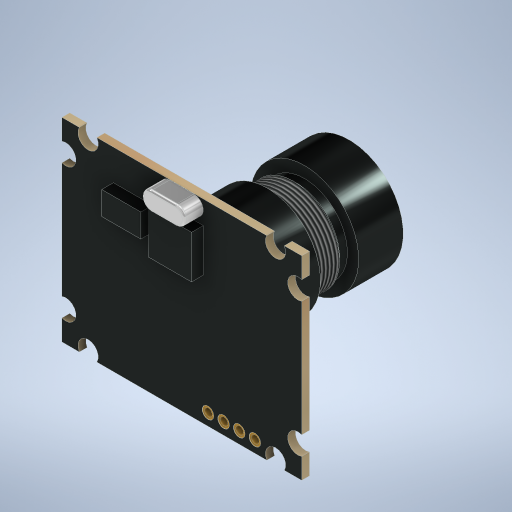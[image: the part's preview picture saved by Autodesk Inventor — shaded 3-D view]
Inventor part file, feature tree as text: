
AUTODESK INVENTOR PART (.ipt)
format: ipt  version: 2023 (Build 270158000, 158)  size: 500,224 bytes
history: native  units: mm
features: extrude x7, sketch x6, fillet x1, revolve x1, thread x1, plane x1, mirror x1
ambient origin geometry x8: Origin, YZ Plane, XZ Plane, XY Plane, X Axis, Y Axis, Z Axis, Center Point
bodies: Solid1 (feature_tree)
feature tree (18):
  extrude  "Extrusion1"  Depth=24.9mm
  sketch  "Sketch2"  dims[d2=2.6mm d3=14.85mm]
  extrude  "Extrusion2"  Depth=14.85mm
  extrude  "Extrusion3"  Depth=2.6mm
  fillet  "Fillet1"  Radius=11.8mm
  sketch  "Sketch3"  dims[d4=8.6mm d5=2.6mm d6=11.8mm]
  sketch  "Sketch4"  dims[d7=12.0mm d8=14.8mm]
  extrude  "Extrusion4"  Depth=14.8mm
  revolve  "Revolution1"  [1 undecoded]
  thread  "Thread1"  [1 undecoded]
  sketch  "Sketch6"  dims[d12=2.224167mm d13=2.65mm d14=14.8mm d15=2.65mm d16=21.748334mm d17=2.224167mm d18=2.65mm d19=1.0mm d20=0.0mm d21=5.5mm d22=5.5mm d23=4.0mm d24=0.0mm d25=1.0mm d26=5.0mm d27=3.0mm d28=1.0mm d29=1.2mm d30=1.5mm d31=0.0mm d32=2.4mm d33=0.0mm d34=0.3mm d36=0.05mm d37=12.8mm d38=12.8mm d39=3.7mm d40=8.9mm d41=1.5mm d42=1.5mm d43=2.5mm d44=0.0mm d45=13.7mm d46=11.8mm d47=11.0mm d48=13.9mm d49=1.6mm d50=9.9mm d51=5.7mm d52=20.4mm d53=1.0mm d54=135.0deg d56=19.5mm d57=90.0deg d58=4.4mm d59=0.0mm d60=1.0mm d61=1.5mm d62=1.5mm d63=6.0mm d64=40.0mm d66=2.0mm d67=10.0mm d69=10.0mm d71=0.0mm d72=0.0mm d73=0.05mm d74=0.0mm d75=2.0mm d76=0.0mm]
  extrude  "Extrusion5"  Depth=2.65mm
  extrude  "Extrusion6"  Depth=2.0mm
  plane  "Work Plane1"
  mirror  "Mirror1"
  extrude  "Extrusion7"  Depth=2.65mm
  sketch  "Sketch1"  dims[d0=30.7mm d1=24.9mm]
  sketch  "Sketch5"  dims[d9=2.65mm d10=2.224167mm d11=21.748334mm]
note: 2 required parameter values undecoded (feature->parameter linkage not recoverable at this tier; creation-order binding heuristic only, values carry confidence <= 0.55)